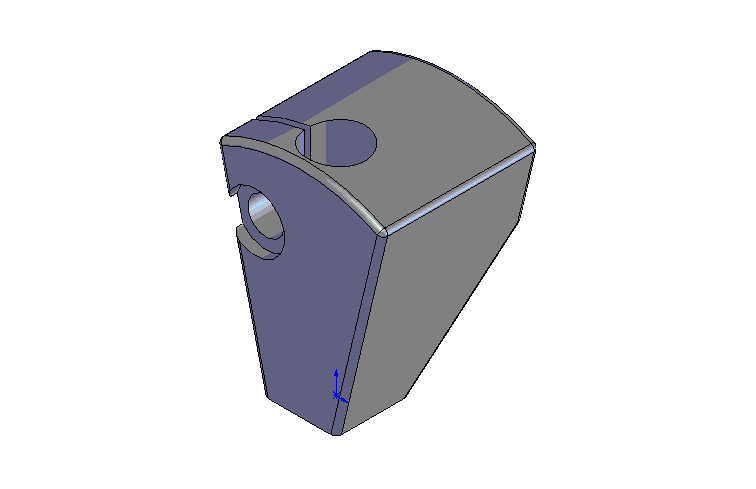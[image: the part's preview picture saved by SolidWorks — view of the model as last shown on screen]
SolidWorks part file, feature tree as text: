
SOLIDWORKS PART (.sldprt)
format: sldprt  version: not decoded by parser v0  size: 334,336 bytes
history: native  units: mm
features: sketch x7, cut_extrude x6, plane x3, material x1, extrude x1, fillet x1 (+10 scaffold rows collapsed)
feature tree (29):
  scaffold x10  (default folders/planes/origin — collapsed)
  material  "Matériau <non spécifié>"
  plane  "Plan de face"
  plane  "Plan de dessus"
  plane  "Plan de droite"
  sketch  "Esquisse1"  dims[D1=21.0mm D2=3.5mm D3=11.5mm D4=12.0mm D5=~10.430688mm]
  extrude  "Extrusion1"  Depth=16mm
  sketch  "Esquisse2"  dims[D1=2.0mm D2=7.0mm]
  cut_extrude  "Enlèv. mat.-Extru.1"  [1 undecoded]
  fillet  "Congé1"  Radius=0.5mm
  sketch  "Esquisse3"  dims[D1=5.5mm]
  cut_extrude  "Enlèv. mat.-Extru.3"  [1 undecoded]
  sketch  "Esquisse4"  dims[D1=0.6mm]
  cut_extrude  "Enlèv. mat.-Extru.4"  [1 undecoded]
  sketch  "Esquisse5"  dims[D1=2.5mm D2=14.0mm D3=4.2mm]
  cut_extrude  "Enlèv. mat.-Extru.5"  Depth=14mm
  sketch  "Esquisse7"  dims[D1=3.5mm]
  cut_extrude  "Enlèv. mat.-Extru.7"  [1 undecoded]
  sketch  "Esquisse6"  dims[D1=5.6mm]
  cut_extrude  "Enlèv. mat.-Extru.6"  Depth=1mm
decode coverage: 11 of 15 modeling features carry decoded parameters
note: ~ marks probable driven/reference dimensions
note: 4 parameter values undecoded
summary: no parameter record found for 4 features
note: suppression state not decoded; provenance and decode notes live in map.json
